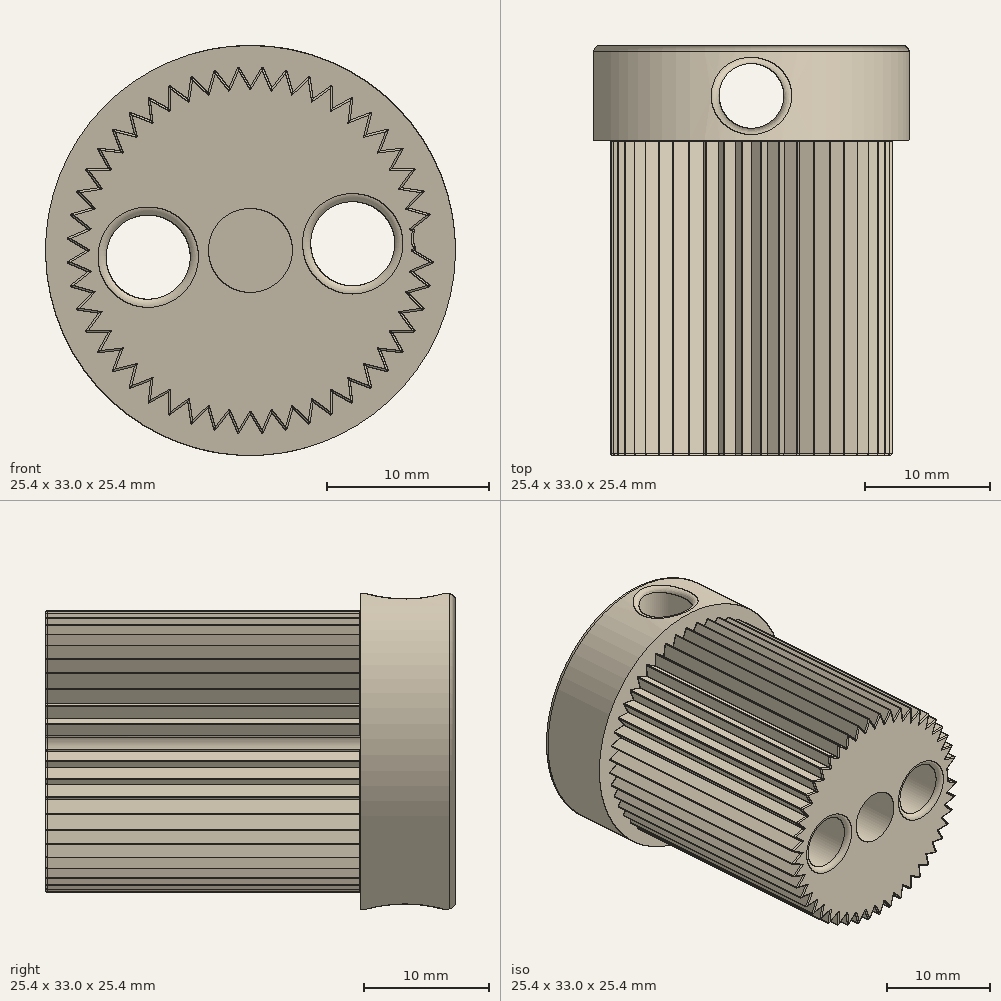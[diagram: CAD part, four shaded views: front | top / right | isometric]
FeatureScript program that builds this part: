
annotation { "Feature Type Name" : "Feature", "Feature Type Description" : "" }
export const myFeature = defineFeature(function(context is Context, id is Id, definition is map)
    precondition{}
    {
        {
            var Q0;
            Q0=qCreatedBy(makeId("Front.planeOp"),FACE);
            var sketch = newSketch(context, id + "F0", { "sketchPlane" : qUnion([Q0])});
            skCircle(sketch, "E0", {"center": v(0, 0) * mm, "radius": 10.16 * mm, "construction": true});
            skCircle(sketch, "E1", {"center": v(0, 0) * mm, "radius": 11.43 * mm, "construction": true});
            skLineSegment(sketch, "E2", {"start": v(0, 0) * mm, "end": v(24.31, 0) * mm, "construction": true});
            skLineSegment(sketch, "E3", {"start": v(0, 0) * mm, "end": v(24.33, -1.6) * mm, "construction": true});
            skLineSegment(sketch, "E4", {"start": v(0, 0) * mm, "end": v(10.07, -1.33) * mm, "construction": true});
            skLineSegment(sketch, "E5", {"start": v(9.53, 0) * mm, "end": v(10.16, 0) * mm});
            skLineSegment(sketch, "E6", {"start": v(10.16, 0) * mm, "end": v(11.4, -0.75) * mm});
            skLineSegment(sketch, "E7", {"start": v(10.07, -1.33) * mm, "end": v(9.44, -1.24) * mm});
            skLineSegment(sketch, "E8", {"start": v(0, 0) * mm, "end": v(9.53, 0) * mm});
            skLineSegment(sketch, "E9", {"start": v(0, 0) * mm, "end": v(9.44, -1.24) * mm});
            skLineSegment(sketch, "E10", {"start": v(11.4, -0.75) * mm, "end": v(10.07, -1.33) * mm});
            skLineSegment(sketch, "E11.trimOffspring", {"start": v(11.33, -1.5) * mm, "end": v(23.43, -3.08) * mm, "construction": true});
            skPoint(sketch, "E12.orphan", {"position": v(10.16, -1.34) * mm});
            skLineSegment(sketch, "E13", {"start": v(17.07, 1.12) * mm, "end": v(-16.43, -1.08) * mm, "construction": true});
            skCircle(sketch, "E14", {"center": v(0, 0) * mm, "radius": 6.35 * mm, "construction": true});
            skCircle(sketch, "E15", {"center": v(-6.34, -0.42) * mm, "radius": 2.6 * mm});
            skCircle(sketch, "E16", {"center": v(6.34, 0.42) * mm, "radius": 2.6 * mm});
            skSolve(sketch);
        }
        {
            var Q0;
            Q0=makeQuery(id+"F0.imprint","IMPRINT",FACE,{"disambiguationData":[TD([[makeQuery(id+"F0.imprint","IMPRINT",EDGE,{"derivedFrom":sQuery(id+"F0.wireOp",EDGE,"E5")}),-1.0]])]});
            var Q1;
            {var subQ0=sQuery(id+"F0.wireOp",EDGE,"E16");var subQ1=sQuery(id+"F0.wireOp",EDGE,"E8");var subQ2=makeQuery(id+"F0.imprint","INTERSECT",VERTEX,{"disambiguationData":[OD(0.0)],"derivedFrom":[subQ1,subQ0]});Q1=makeQuery(id+"F0.imprint","IMPRINT",FACE,{"disambiguationData":[TD([[makeQuery(id+"F0.imprint","IMPRINT",EDGE,{"disambiguationData":[TD([[subQ2,-1.0]])],"derivedFrom":subQ1}),-1.0]])]});}
            var Q2;
            {var subQ0=sQuery(id+"F0.wireOp",EDGE,"E9");var subQ1=sQuery(id+"F0.wireOp",EDGE,"E8");var subQ2=makeQuery(id+"F0.imprint","INTERSECT",VERTEX,{"derivedFrom":[subQ1,subQ0]});Q2=makeQuery(id+"F0.imprint","IMPRINT",FACE,{"disambiguationData":[TD([[makeQuery(id+"F0.imprint","IMPRINT",EDGE,{"disambiguationData":[TD([[subQ2,-1.0]])],"derivedFrom":subQ1}),-1.0]])]});}
            extrude(context, id + "F1", {"entities" : qUnion([Q0, Q1, Q2]), "depth" : 25.4 * mm});
        }
        {
            var Q0;
            Q0=makeQuery(id+"F1.opExtrude","CAP_EDGE",EDGE,{"disambiguationData":[OSD([sQuery(id+"F0.wireOp",EDGE,"E6")])],"isStart":false});
            var Q1;
            Q1=makeQuery(id+"F1.opExtrude","CAP_EDGE",EDGE,{"disambiguationData":[OSD([sQuery(id+"F0.wireOp",EDGE,"E10")])],"isStart":false});
            var Q2;
            Q2=makeQuery(id+"F1.opExtrude","CAP_EDGE",EDGE,{"disambiguationData":[OSD([sQuery(id+"F0.wireOp",EDGE,"E6")])],"isStart":true});
            var Q3;
            Q3=makeQuery(id+"F1.opExtrude","CAP_EDGE",EDGE,{"disambiguationData":[OSD([sQuery(id+"F0.wireOp",EDGE,"E10")])],"isStart":true});
            fillet(context, id + "F2", {"entities" : qUnion([Q0, Q1, Q2, Q3]), "radius" : 0.13 * mm, "tangentPropagation" : true, "allowEdgeOverflow" : false});
        }
        {
            var Q0;
            Q0=makeQuery(id+"F1.opExtrude","SWEPT_EDGE",EDGE,{"disambiguationData":[OSD([sQuery(id+"F0.wireOp",EDGE,"E6"),sQuery(id+"F0.wireOp",EDGE,"E10")])]});
            fillet(context, id + "F3", {"entities" : qUnion([Q0]), "radius" : 0.05 * mm, "tangentPropagation" : true, "allowEdgeOverflow" : false});
        }
        {
            var Q0;
            Q0=makeQuery(id+"F1.opExtrude","SWEPT_BODY",BODY,{"disambiguationData":[OSD([sQuery(id+"F0.wireOp",EDGE,"E5"),sQuery(id+"F0.wireOp",EDGE,"E6"),sQuery(id+"F0.wireOp",EDGE,"gNua0P1m-RBOV-57z6-Uz5b-c0gyhJW3q2aB"),sQuery(id+"F0.wireOp",EDGE,"E7"),sQuery(id+"F0.wireOp",EDGE,"E8"),sQuery(id+"F0.wireOp",EDGE,"E9")])]});
            var Q1;
            Q1=makeQuery(id+"F1.opExtrude","SWEPT_EDGE",EDGE,{"disambiguationData":[OSD([sQuery(id+"F0.wireOp",EDGE,"E8"),sQuery(id+"F0.wireOp",EDGE,"E9")])]});
            circularPattern(context, id + "F4", {"operationType" : NewBodyOperationType.ADD, "entities" : qUnion([Q0]), "axis" : qUnion([Q1]), "angle" : 360 * degree, "instanceCount" : 48, "equalSpace" : true});
        }
        {
            var Q0;
            {var subQ0=makeQuery(id+"F1.opExtrude","CAP_FACE",FACE,{"disambiguationData":[OSD([sQuery(id+"F0.wireOp",EDGE,"E5"),sQuery(id+"F0.wireOp",EDGE,"E6"),sQuery(id+"F0.wireOp",EDGE,"E7"),sQuery(id+"F0.wireOp",EDGE,"E8"),sQuery(id+"F0.wireOp",EDGE,"E9"),sQuery(id+"F0.wireOp",EDGE,"E10")])],"isStart":true});Q0=makeQuery(id+"F4.boolean.opBoolean","MERGE",FACE,{"derivedFrom":[subQ0,makeQuery(id+"F4.opPattern","COPY",FACE,{"derivedFrom":subQ0,"instanceName":"1"}),makeQuery(id+"F4.opPattern","COPY",FACE,{"derivedFrom":subQ0,"instanceName":"2"}),makeQuery(id+"F4.opPattern","COPY",FACE,{"derivedFrom":subQ0,"instanceName":"3"}),makeQuery(id+"F4.opPattern","COPY",FACE,{"derivedFrom":subQ0,"instanceName":"4"}),makeQuery(id+"F4.opPattern","COPY",FACE,{"derivedFrom":subQ0,"instanceName":"5"}),makeQuery(id+"F4.opPattern","COPY",FACE,{"derivedFrom":subQ0,"instanceName":"6"}),makeQuery(id+"F4.opPattern","COPY",FACE,{"derivedFrom":subQ0,"instanceName":"7"}),makeQuery(id+"F4.opPattern","COPY",FACE,{"derivedFrom":subQ0,"instanceName":"8"}),makeQuery(id+"F4.opPattern","COPY",FACE,{"derivedFrom":subQ0,"instanceName":"9"}),makeQuery(id+"F4.opPattern","COPY",FACE,{"derivedFrom":subQ0,"instanceName":"10"}),makeQuery(id+"F4.opPattern","COPY",FACE,{"derivedFrom":subQ0,"instanceName":"11"}),makeQuery(id+"F4.opPattern","COPY",FACE,{"derivedFrom":subQ0,"instanceName":"12"}),makeQuery(id+"F4.opPattern","COPY",FACE,{"derivedFrom":subQ0,"instanceName":"13"}),makeQuery(id+"F4.opPattern","COPY",FACE,{"derivedFrom":subQ0,"instanceName":"14"}),makeQuery(id+"F4.opPattern","COPY",FACE,{"derivedFrom":subQ0,"instanceName":"15"}),makeQuery(id+"F4.opPattern","COPY",FACE,{"derivedFrom":subQ0,"instanceName":"16"}),makeQuery(id+"F4.opPattern","COPY",FACE,{"derivedFrom":subQ0,"instanceName":"17"}),makeQuery(id+"F4.opPattern","COPY",FACE,{"derivedFrom":subQ0,"instanceName":"18"}),makeQuery(id+"F4.opPattern","COPY",FACE,{"derivedFrom":subQ0,"instanceName":"19"}),makeQuery(id+"F4.opPattern","COPY",FACE,{"derivedFrom":subQ0,"instanceName":"20"}),makeQuery(id+"F4.opPattern","COPY",FACE,{"derivedFrom":subQ0,"instanceName":"21"}),makeQuery(id+"F4.opPattern","COPY",FACE,{"derivedFrom":subQ0,"instanceName":"22"}),makeQuery(id+"F4.opPattern","COPY",FACE,{"derivedFrom":subQ0,"instanceName":"23"}),makeQuery(id+"F4.opPattern","COPY",FACE,{"derivedFrom":subQ0,"instanceName":"24"}),makeQuery(id+"F4.opPattern","COPY",FACE,{"derivedFrom":subQ0,"instanceName":"25"}),makeQuery(id+"F4.opPattern","COPY",FACE,{"derivedFrom":subQ0,"instanceName":"26"}),makeQuery(id+"F4.opPattern","COPY",FACE,{"derivedFrom":subQ0,"instanceName":"27"}),makeQuery(id+"F4.opPattern","COPY",FACE,{"derivedFrom":subQ0,"instanceName":"28"}),makeQuery(id+"F4.opPattern","COPY",FACE,{"derivedFrom":subQ0,"instanceName":"29"}),makeQuery(id+"F4.opPattern","COPY",FACE,{"derivedFrom":subQ0,"instanceName":"30"}),makeQuery(id+"F4.opPattern","COPY",FACE,{"derivedFrom":subQ0,"instanceName":"31"}),makeQuery(id+"F4.opPattern","COPY",FACE,{"derivedFrom":subQ0,"instanceName":"32"}),makeQuery(id+"F4.opPattern","COPY",FACE,{"derivedFrom":subQ0,"instanceName":"33"}),makeQuery(id+"F4.opPattern","COPY",FACE,{"derivedFrom":subQ0,"instanceName":"34"}),makeQuery(id+"F4.opPattern","COPY",FACE,{"derivedFrom":subQ0,"instanceName":"35"}),makeQuery(id+"F4.opPattern","COPY",FACE,{"derivedFrom":subQ0,"instanceName":"36"}),makeQuery(id+"F4.opPattern","COPY",FACE,{"derivedFrom":subQ0,"instanceName":"37"}),makeQuery(id+"F4.opPattern","COPY",FACE,{"derivedFrom":subQ0,"instanceName":"38"}),makeQuery(id+"F4.opPattern","COPY",FACE,{"derivedFrom":subQ0,"instanceName":"39"}),makeQuery(id+"F4.opPattern","COPY",FACE,{"derivedFrom":subQ0,"instanceName":"40"}),makeQuery(id+"F4.opPattern","COPY",FACE,{"derivedFrom":subQ0,"instanceName":"41"}),makeQuery(id+"F4.opPattern","COPY",FACE,{"derivedFrom":subQ0,"instanceName":"42"}),makeQuery(id+"F4.opPattern","COPY",FACE,{"derivedFrom":subQ0,"instanceName":"43"}),makeQuery(id+"F4.opPattern","COPY",FACE,{"derivedFrom":subQ0,"instanceName":"44"}),makeQuery(id+"F4.opPattern","COPY",FACE,{"derivedFrom":subQ0,"instanceName":"45"}),makeQuery(id+"F4.opPattern","COPY",FACE,{"derivedFrom":subQ0,"instanceName":"46"}),makeQuery(id+"F4.opPattern","COPY",FACE,{"derivedFrom":subQ0,"instanceName":"47"})]});}
            var sketch = newSketch(context, id + "F5", { "sketchPlane" : qUnion([Q0])});
            skCircle(sketch, "E17", {"center": v(0, 0) * mm, "radius": 12.7 * mm});
            skSolve(sketch);
        }
        {
            var Q0;
            Q0=makeQuery(id+"F5.imprint","IMPRINT",FACE,{"disambiguationData":[TD([[makeQuery(id+"F5.imprint","IMPRINT",EDGE,{"derivedFrom":sQuery(id+"F5.wireOp",EDGE,"E17")}),1.0]])]});
            var Q1;
            {var subQ0=sQuery(id+"F0.wireOp",EDGE,"E10");var subQ1=sQuery(id+"F0.wireOp",EDGE,"E6");var subQ2=makeQuery(id+"F1.opExtrude","CAP_FACE",FACE,{"disambiguationData":[OSD([sQuery(id+"F0.wireOp",EDGE,"E5"),subQ1,sQuery(id+"F0.wireOp",EDGE,"E7"),sQuery(id+"F0.wireOp",EDGE,"E8"),sQuery(id+"F0.wireOp",EDGE,"E9"),subQ0])],"isStart":true});var subQ4=makeQuery(id+"F2.opFillet","BLEND_EDGE",EDGE,{"blendedFrom":[makeQuery(id+"F1.opExtrude","CAP_EDGE",EDGE,{"disambiguationData":[OSD([subQ1])],"isStart":true}),subQ2],"blendedInto":[subQ2]});Q1=makeQuery(id+"F5.imprint","IMPRINT",FACE,{"disambiguationData":[TD([[makeQuery(id+"F5.imprint","IMPRINT",EDGE,{"derivedFrom":subQ4}),1.0]])]});}
            var Q2;
            Q2=sQuery(id+"F5.wireOp",EDGE,"E17");
            extrude(context, id + "F6", {"entities" : qUnion([Q0, Q1]), "operationType" : NewBodyOperationType.ADD, "surfaceEntities" : qUnion([Q2]), "depth" : 7.62 * mm});
        }
        {
            var Q0;
            Q0=makeQuery(id+"F0.imprint","IMPRINT",FACE,{"disambiguationData":[TD([[makeQuery(id+"F0.imprint","IMPRINT",EDGE,{"derivedFrom":sQuery(id+"F0.wireOp",EDGE,"E15")}),1.0]])]});
            var Q1;
            {var subQ0=sQuery(id+"F0.wireOp",EDGE,"E16");var subQ1=sQuery(id+"F0.wireOp",EDGE,"E8");var subQ2=makeQuery(id+"F0.imprint","INTERSECT",VERTEX,{"disambiguationData":[OD(0.0)],"derivedFrom":[subQ1,subQ0]});Q1=makeQuery(id+"F0.imprint","IMPRINT",FACE,{"disambiguationData":[TD([[makeQuery(id+"F0.imprint","IMPRINT",EDGE,{"disambiguationData":[TD([[subQ2,-1.0]])],"derivedFrom":subQ1}),1.0]])]});}
            var Q2;
            {var subQ0=sQuery(id+"F0.wireOp",EDGE,"E16");var subQ1=sQuery(id+"F0.wireOp",EDGE,"E8");var subQ2=makeQuery(id+"F0.imprint","INTERSECT",VERTEX,{"disambiguationData":[OD(0.0)],"derivedFrom":[subQ1,subQ0]});Q2=makeQuery(id+"F0.imprint","IMPRINT",FACE,{"disambiguationData":[TD([[makeQuery(id+"F0.imprint","IMPRINT",EDGE,{"disambiguationData":[TD([[subQ2,-1.0]])],"derivedFrom":subQ1}),-1.0]])]});}
            var Q3;
            {var subQ0=sQuery(id+"F0.wireOp",EDGE,"E16");var subQ1=sQuery(id+"F0.wireOp",EDGE,"E9");var subQ2=makeQuery(id+"F0.imprint","INTERSECT",VERTEX,{"disambiguationData":[OD(0.0)],"derivedFrom":[subQ1,subQ0]});Q3=makeQuery(id+"F0.imprint","IMPRINT",FACE,{"disambiguationData":[TD([[makeQuery(id+"F0.imprint","IMPRINT",EDGE,{"disambiguationData":[TD([[subQ2,-1.0]])],"derivedFrom":subQ1}),-1.0]])]});}
            extrude(context, id + "F7", {"entities" : qUnion([Q0, Q1, Q2, Q3]), "operationType" : NewBodyOperationType.REMOVE, "endBound" : BoundingType.SYMMETRIC, "depth" : 50.8 * mm});
        }
        {
            var Q0;
            {var subQ0=makeQuery(id+"F1.opExtrude","CAP_FACE",FACE,{"disambiguationData":[OSD([sQuery(id+"F0.wireOp",EDGE,"E5"),sQuery(id+"F0.wireOp",EDGE,"E6"),sQuery(id+"F0.wireOp",EDGE,"gNua0P1m-RBOV-57z6-Uz5b-c0gyhJW3q2aB"),sQuery(id+"F0.wireOp",EDGE,"E7"),sQuery(id+"F0.wireOp",EDGE,"E8"),sQuery(id+"F0.wireOp",EDGE,"E9")])],"isStart":false});Q0=makeQuery(id+"F4.boolean.opBoolean","MERGE",FACE,{"derivedFrom":[subQ0,makeQuery(id+"F4.opPattern","COPY",FACE,{"derivedFrom":subQ0,"instanceName":"1"}),makeQuery(id+"F4.opPattern","COPY",FACE,{"derivedFrom":subQ0,"instanceName":"2"}),makeQuery(id+"F4.opPattern","COPY",FACE,{"derivedFrom":subQ0,"instanceName":"3"}),makeQuery(id+"F4.opPattern","COPY",FACE,{"derivedFrom":subQ0,"instanceName":"4"}),makeQuery(id+"F4.opPattern","COPY",FACE,{"derivedFrom":subQ0,"instanceName":"5"}),makeQuery(id+"F4.opPattern","COPY",FACE,{"derivedFrom":subQ0,"instanceName":"6"}),makeQuery(id+"F4.opPattern","COPY",FACE,{"derivedFrom":subQ0,"instanceName":"7"}),makeQuery(id+"F4.opPattern","COPY",FACE,{"derivedFrom":subQ0,"instanceName":"8"}),makeQuery(id+"F4.opPattern","COPY",FACE,{"derivedFrom":subQ0,"instanceName":"9"}),makeQuery(id+"F4.opPattern","COPY",FACE,{"derivedFrom":subQ0,"instanceName":"10"}),makeQuery(id+"F4.opPattern","COPY",FACE,{"derivedFrom":subQ0,"instanceName":"11"}),makeQuery(id+"F4.opPattern","COPY",FACE,{"derivedFrom":subQ0,"instanceName":"12"}),makeQuery(id+"F4.opPattern","COPY",FACE,{"derivedFrom":subQ0,"instanceName":"13"}),makeQuery(id+"F4.opPattern","COPY",FACE,{"derivedFrom":subQ0,"instanceName":"14"}),makeQuery(id+"F4.opPattern","COPY",FACE,{"derivedFrom":subQ0,"instanceName":"15"}),makeQuery(id+"F4.opPattern","COPY",FACE,{"derivedFrom":subQ0,"instanceName":"16"}),makeQuery(id+"F4.opPattern","COPY",FACE,{"derivedFrom":subQ0,"instanceName":"17"}),makeQuery(id+"F4.opPattern","COPY",FACE,{"derivedFrom":subQ0,"instanceName":"18"}),makeQuery(id+"F4.opPattern","COPY",FACE,{"derivedFrom":subQ0,"instanceName":"19"}),makeQuery(id+"F4.opPattern","COPY",FACE,{"derivedFrom":subQ0,"instanceName":"20"}),makeQuery(id+"F4.opPattern","COPY",FACE,{"derivedFrom":subQ0,"instanceName":"21"}),makeQuery(id+"F4.opPattern","COPY",FACE,{"derivedFrom":subQ0,"instanceName":"22"}),makeQuery(id+"F4.opPattern","COPY",FACE,{"derivedFrom":subQ0,"instanceName":"23"}),makeQuery(id+"F4.opPattern","COPY",FACE,{"derivedFrom":subQ0,"instanceName":"24"}),makeQuery(id+"F4.opPattern","COPY",FACE,{"derivedFrom":subQ0,"instanceName":"25"}),makeQuery(id+"F4.opPattern","COPY",FACE,{"derivedFrom":subQ0,"instanceName":"26"}),makeQuery(id+"F4.opPattern","COPY",FACE,{"derivedFrom":subQ0,"instanceName":"27"}),makeQuery(id+"F4.opPattern","COPY",FACE,{"derivedFrom":subQ0,"instanceName":"28"}),makeQuery(id+"F4.opPattern","COPY",FACE,{"derivedFrom":subQ0,"instanceName":"29"}),makeQuery(id+"F4.opPattern","COPY",FACE,{"derivedFrom":subQ0,"instanceName":"30"}),makeQuery(id+"F4.opPattern","COPY",FACE,{"derivedFrom":subQ0,"instanceName":"31"}),makeQuery(id+"F4.opPattern","COPY",FACE,{"derivedFrom":subQ0,"instanceName":"32"}),makeQuery(id+"F4.opPattern","COPY",FACE,{"derivedFrom":subQ0,"instanceName":"33"}),makeQuery(id+"F4.opPattern","COPY",FACE,{"derivedFrom":subQ0,"instanceName":"34"}),makeQuery(id+"F4.opPattern","COPY",FACE,{"derivedFrom":subQ0,"instanceName":"35"}),makeQuery(id+"F4.opPattern","COPY",FACE,{"derivedFrom":subQ0,"instanceName":"36"}),makeQuery(id+"F4.opPattern","COPY",FACE,{"derivedFrom":subQ0,"instanceName":"37"}),makeQuery(id+"F4.opPattern","COPY",FACE,{"derivedFrom":subQ0,"instanceName":"38"}),makeQuery(id+"F4.opPattern","COPY",FACE,{"derivedFrom":subQ0,"instanceName":"39"}),makeQuery(id+"F4.opPattern","COPY",FACE,{"derivedFrom":subQ0,"instanceName":"40"}),makeQuery(id+"F4.opPattern","COPY",FACE,{"derivedFrom":subQ0,"instanceName":"41"}),makeQuery(id+"F4.opPattern","COPY",FACE,{"derivedFrom":subQ0,"instanceName":"42"}),makeQuery(id+"F4.opPattern","COPY",FACE,{"derivedFrom":subQ0,"instanceName":"43"}),makeQuery(id+"F4.opPattern","COPY",FACE,{"derivedFrom":subQ0,"instanceName":"44"}),makeQuery(id+"F4.opPattern","COPY",FACE,{"derivedFrom":subQ0,"instanceName":"45"}),makeQuery(id+"F4.opPattern","COPY",FACE,{"derivedFrom":subQ0,"instanceName":"46"}),makeQuery(id+"F4.opPattern","COPY",FACE,{"derivedFrom":subQ0,"instanceName":"47"}),makeQuery(id+"F4.opPattern","COPY",FACE,{"derivedFrom":subQ0,"instanceName":"48"}),makeQuery(id+"F4.opPattern","COPY",FACE,{"derivedFrom":subQ0,"instanceName":"49"}),makeQuery(id+"F4.opPattern","COPY",FACE,{"derivedFrom":subQ0,"instanceName":"50"}),makeQuery(id+"F4.opPattern","COPY",FACE,{"derivedFrom":subQ0,"instanceName":"51"}),makeQuery(id+"F4.opPattern","COPY",FACE,{"derivedFrom":subQ0,"instanceName":"52"}),makeQuery(id+"F4.opPattern","COPY",FACE,{"derivedFrom":subQ0,"instanceName":"53"}),makeQuery(id+"F4.opPattern","COPY",FACE,{"derivedFrom":subQ0,"instanceName":"54"}),makeQuery(id+"F4.opPattern","COPY",FACE,{"derivedFrom":subQ0,"instanceName":"55"}),makeQuery(id+"F4.opPattern","COPY",FACE,{"derivedFrom":subQ0,"instanceName":"56"}),makeQuery(id+"F4.opPattern","COPY",FACE,{"derivedFrom":subQ0,"instanceName":"57"}),makeQuery(id+"F4.opPattern","COPY",FACE,{"derivedFrom":subQ0,"instanceName":"58"}),makeQuery(id+"F4.opPattern","COPY",FACE,{"derivedFrom":subQ0,"instanceName":"59"}),makeQuery(id+"F4.opPattern","COPY",FACE,{"derivedFrom":subQ0,"instanceName":"60"}),makeQuery(id+"F4.opPattern","COPY",FACE,{"derivedFrom":subQ0,"instanceName":"61"}),makeQuery(id+"F4.opPattern","COPY",FACE,{"derivedFrom":subQ0,"instanceName":"62"}),makeQuery(id+"F4.opPattern","COPY",FACE,{"derivedFrom":subQ0,"instanceName":"63"}),makeQuery(id+"F4.opPattern","COPY",FACE,{"derivedFrom":subQ0,"instanceName":"64"}),makeQuery(id+"F4.opPattern","COPY",FACE,{"derivedFrom":subQ0,"instanceName":"65"}),makeQuery(id+"F4.opPattern","COPY",FACE,{"derivedFrom":subQ0,"instanceName":"66"}),makeQuery(id+"F4.opPattern","COPY",FACE,{"derivedFrom":subQ0,"instanceName":"67"}),makeQuery(id+"F4.opPattern","COPY",FACE,{"derivedFrom":subQ0,"instanceName":"68"}),makeQuery(id+"F4.opPattern","COPY",FACE,{"derivedFrom":subQ0,"instanceName":"69"}),makeQuery(id+"F4.opPattern","COPY",FACE,{"derivedFrom":subQ0,"instanceName":"70"}),makeQuery(id+"F4.opPattern","COPY",FACE,{"derivedFrom":subQ0,"instanceName":"71"})]});}
            var sketch = newSketch(context, id + "F8", { "sketchPlane" : qUnion([Q0])});
            skCircle(sketch, "E18", {"center": v(0, 0) * mm, "radius": 9.59 * mm});
            skLineSegment(sketch, "E19", {"start": v(0, 0) * mm, "end": v(11.91, 0) * mm, "construction": true});
            skLineSegment(sketch, "E20", {"start": v(0, 0) * mm, "end": v(12.83, 0.84) * mm, "construction": true});
            skCircle(sketch, "E21", {"center": v(10.07, 0.66) * mm, "radius": 0.5 * mm});
            skCircle(sketch, "E22", {"center": v(0, 0) * mm, "radius": 2.6 * mm});
            skSolve(sketch);
        }
        {
            var Q0;
            {var subQ0=makeQuery(id+"F1.opExtrude","CAP_FACE",FACE,{"disambiguationData":[OSD([sQuery(id+"F0.wireOp",EDGE,"E5"),sQuery(id+"F0.wireOp",EDGE,"E6"),sQuery(id+"F0.wireOp",EDGE,"E7"),sQuery(id+"F0.wireOp",EDGE,"E8"),sQuery(id+"F0.wireOp",EDGE,"E9"),sQuery(id+"F0.wireOp",EDGE,"E10")])],"isStart":false});Q0=makeQuery(id+"F4.boolean.opBoolean","MERGE",FACE,{"derivedFrom":[subQ0,makeQuery(id+"F4.opPattern","COPY",FACE,{"derivedFrom":subQ0,"instanceName":"1"}),makeQuery(id+"F4.opPattern","COPY",FACE,{"derivedFrom":subQ0,"instanceName":"2"}),makeQuery(id+"F4.opPattern","COPY",FACE,{"derivedFrom":subQ0,"instanceName":"3"}),makeQuery(id+"F4.opPattern","COPY",FACE,{"derivedFrom":subQ0,"instanceName":"4"}),makeQuery(id+"F4.opPattern","COPY",FACE,{"derivedFrom":subQ0,"instanceName":"5"}),makeQuery(id+"F4.opPattern","COPY",FACE,{"derivedFrom":subQ0,"instanceName":"6"}),makeQuery(id+"F4.opPattern","COPY",FACE,{"derivedFrom":subQ0,"instanceName":"7"}),makeQuery(id+"F4.opPattern","COPY",FACE,{"derivedFrom":subQ0,"instanceName":"8"}),makeQuery(id+"F4.opPattern","COPY",FACE,{"derivedFrom":subQ0,"instanceName":"9"}),makeQuery(id+"F4.opPattern","COPY",FACE,{"derivedFrom":subQ0,"instanceName":"10"}),makeQuery(id+"F4.opPattern","COPY",FACE,{"derivedFrom":subQ0,"instanceName":"11"}),makeQuery(id+"F4.opPattern","COPY",FACE,{"derivedFrom":subQ0,"instanceName":"12"}),makeQuery(id+"F4.opPattern","COPY",FACE,{"derivedFrom":subQ0,"instanceName":"13"}),makeQuery(id+"F4.opPattern","COPY",FACE,{"derivedFrom":subQ0,"instanceName":"14"}),makeQuery(id+"F4.opPattern","COPY",FACE,{"derivedFrom":subQ0,"instanceName":"15"}),makeQuery(id+"F4.opPattern","COPY",FACE,{"derivedFrom":subQ0,"instanceName":"16"}),makeQuery(id+"F4.opPattern","COPY",FACE,{"derivedFrom":subQ0,"instanceName":"17"}),makeQuery(id+"F4.opPattern","COPY",FACE,{"derivedFrom":subQ0,"instanceName":"18"}),makeQuery(id+"F4.opPattern","COPY",FACE,{"derivedFrom":subQ0,"instanceName":"19"}),makeQuery(id+"F4.opPattern","COPY",FACE,{"derivedFrom":subQ0,"instanceName":"20"}),makeQuery(id+"F4.opPattern","COPY",FACE,{"derivedFrom":subQ0,"instanceName":"21"}),makeQuery(id+"F4.opPattern","COPY",FACE,{"derivedFrom":subQ0,"instanceName":"22"}),makeQuery(id+"F4.opPattern","COPY",FACE,{"derivedFrom":subQ0,"instanceName":"23"}),makeQuery(id+"F4.opPattern","COPY",FACE,{"derivedFrom":subQ0,"instanceName":"24"}),makeQuery(id+"F4.opPattern","COPY",FACE,{"derivedFrom":subQ0,"instanceName":"25"}),makeQuery(id+"F4.opPattern","COPY",FACE,{"derivedFrom":subQ0,"instanceName":"26"}),makeQuery(id+"F4.opPattern","COPY",FACE,{"derivedFrom":subQ0,"instanceName":"27"}),makeQuery(id+"F4.opPattern","COPY",FACE,{"derivedFrom":subQ0,"instanceName":"28"}),makeQuery(id+"F4.opPattern","COPY",FACE,{"derivedFrom":subQ0,"instanceName":"29"}),makeQuery(id+"F4.opPattern","COPY",FACE,{"derivedFrom":subQ0,"instanceName":"30"}),makeQuery(id+"F4.opPattern","COPY",FACE,{"derivedFrom":subQ0,"instanceName":"31"}),makeQuery(id+"F4.opPattern","COPY",FACE,{"derivedFrom":subQ0,"instanceName":"32"}),makeQuery(id+"F4.opPattern","COPY",FACE,{"derivedFrom":subQ0,"instanceName":"33"}),makeQuery(id+"F4.opPattern","COPY",FACE,{"derivedFrom":subQ0,"instanceName":"34"}),makeQuery(id+"F4.opPattern","COPY",FACE,{"derivedFrom":subQ0,"instanceName":"35"}),makeQuery(id+"F4.opPattern","COPY",FACE,{"derivedFrom":subQ0,"instanceName":"36"}),makeQuery(id+"F4.opPattern","COPY",FACE,{"derivedFrom":subQ0,"instanceName":"37"}),makeQuery(id+"F4.opPattern","COPY",FACE,{"derivedFrom":subQ0,"instanceName":"38"}),makeQuery(id+"F4.opPattern","COPY",FACE,{"derivedFrom":subQ0,"instanceName":"39"}),makeQuery(id+"F4.opPattern","COPY",FACE,{"derivedFrom":subQ0,"instanceName":"40"}),makeQuery(id+"F4.opPattern","COPY",FACE,{"derivedFrom":subQ0,"instanceName":"41"}),makeQuery(id+"F4.opPattern","COPY",FACE,{"derivedFrom":subQ0,"instanceName":"42"}),makeQuery(id+"F4.opPattern","COPY",FACE,{"derivedFrom":subQ0,"instanceName":"43"}),makeQuery(id+"F4.opPattern","COPY",FACE,{"derivedFrom":subQ0,"instanceName":"44"}),makeQuery(id+"F4.opPattern","COPY",FACE,{"derivedFrom":subQ0,"instanceName":"45"}),makeQuery(id+"F4.opPattern","COPY",FACE,{"derivedFrom":subQ0,"instanceName":"46"}),makeQuery(id+"F4.opPattern","COPY",FACE,{"derivedFrom":subQ0,"instanceName":"47"})]});}
            var sketch = newSketch(context, id + "F9", { "sketchPlane" : qUnion([Q0])});
            skCircle(sketch, "E23", {"center": v(11.13, 0.73) * mm, "radius": 1.05 * mm});
            skSolve(sketch);
        }
        {
            var Q0;
            Q0=qSketchRegion(id+"F9",true);
            var Q1;
            Q1=makeQuery(id+"F6.opExtrude","CAP_FACE",FACE,{"disambiguationData":[OSD([sQuery(id+"F5.wireOp",EDGE,"E17")])],"isStart":true});
            extrude(context, id + "F10", {"entities" : qUnion([Q0]), "operationType" : NewBodyOperationType.REMOVE, "endBound" : BoundingType.UP_TO_SURFACE, "oppositeDirection" : true, "endBoundEntityFace" : qUnion([Q1]), "depth" : 25.4 * mm});
        }
        {
            var Q0;
            Q0=makeQuery(id+"F8.imprint","IMPRINT",FACE,{"disambiguationData":[TD([[makeQuery(id+"F8.imprint","IMPRINT",EDGE,{"derivedFrom":sQuery(id+"F8.wireOp",EDGE,"E22")}),1.0]])]});
            var Q1;
            Q1=sQuery(id+"F8.wireOp",EDGE,"E22");
            extrude(context, id + "F11", {"entities" : qUnion([Q0]), "operationType" : NewBodyOperationType.REMOVE, "surfaceEntities" : qUnion([Q1]), "oppositeDirection" : true, "depth" : 22.86 * mm});
        }
        {
            var Q0;
            Q0=makeQuery(id+"F10.boolean.opBoolean","INTERSECT",EDGE,{"derivedFrom":[makeQuery(id+"F4.opPattern","COPY",FACE,{"derivedFrom":makeQuery(id+"F1.opExtrude","SWEPT_FACE",FACE,{"disambiguationData":[OSD([sQuery(id+"F0.wireOp",EDGE,"E6")])]}),"instanceName":"47"}),makeQuery(id+"F10.opExtrude","SWEPT_FACE",FACE,{"disambiguationData":[OSD([sQuery(id+"F9.wireOp",EDGE,"E23")])]})]});
            var Q1;
            Q1=makeQuery(id+"F10.boolean.opBoolean","COPY",EDGE,{"derivedFrom":makeQuery(id+"F10.opExtrude","CAP_EDGE",EDGE,{"disambiguationData":[OSD([sQuery(id+"F9.wireOp",EDGE,"E23")])],"isStart":true})});
            fillet(context, id + "F12", {"entities" : qUnion([Q0, Q1]), "radius" : 0.13 * mm, "tangentPropagation" : true, "allowEdgeOverflow" : false});
        }
        {
            var Q0;
            Q0=qCreatedBy(makeId("Top.planeOp"),FACE);
            var sketch = newSketch(context, id + "F13", { "sketchPlane" : qUnion([Q0])});
            skLineSegment(sketch, "E24", {"start": v(-12.7, 0) * mm, "end": v(-12.7, 7.62) * mm});
            skLineSegment(sketch, "E25", {"start": v(12.7, 7.62) * mm, "end": v(12.7, 0) * mm});
            skCircle(sketch, "E26", {"center": v(0, 3.56) * mm, "radius": 2.6 * mm});
            skSolve(sketch);
        }
        {
            var Q0;
            Q0=qSketchRegion(id+"F13",true);
            var Q1;
            Q1=sQuery(id+"F13.wireOp",EDGE,"E26");
            extrude(context, id + "F14", {"entities" : qUnion([Q0]), "operationType" : NewBodyOperationType.REMOVE, "surfaceEntities" : qUnion([Q1]), "endBound" : BoundingType.SYMMETRIC, "oppositeDirection" : true, "depth" : 25.4 * mm});
        }
        {
            var Q0;
            Q0=makeQuery(id+"F7.boolean.opBoolean","COPY",EDGE,{"derivedFrom":makeQuery(id+"F7.opExtrude","CAP_EDGE",EDGE,{"disambiguationData":[OSD([sQuery(id+"F0.wireOp",EDGE,"E16")])],"isStart":true})});
            var Q1;
            Q1=makeQuery(id+"F7.boolean.opBoolean","COPY",EDGE,{"derivedFrom":makeQuery(id+"F7.opExtrude","CAP_EDGE",EDGE,{"disambiguationData":[OSD([sQuery(id+"F0.wireOp",EDGE,"E15")])],"isStart":true})});
            var Q2;
            {var subQ0=makeQuery(id+"F1.opExtrude","CAP_FACE",FACE,{"disambiguationData":[OSD([sQuery(id+"F0.wireOp",EDGE,"E5"),sQuery(id+"F0.wireOp",EDGE,"E6"),sQuery(id+"F0.wireOp",EDGE,"E7"),sQuery(id+"F0.wireOp",EDGE,"E8"),sQuery(id+"F0.wireOp",EDGE,"E9"),sQuery(id+"F0.wireOp",EDGE,"E10")])],"isStart":false});Q2=makeQuery(id+"F7.boolean.opBoolean","INTERSECT",EDGE,{"derivedFrom":[makeQuery(id+"F4.boolean.opBoolean","MERGE",FACE,{"derivedFrom":[subQ0,makeQuery(id+"F4.opPattern","COPY",FACE,{"derivedFrom":subQ0,"instanceName":"1"}),makeQuery(id+"F4.opPattern","COPY",FACE,{"derivedFrom":subQ0,"instanceName":"2"}),makeQuery(id+"F4.opPattern","COPY",FACE,{"derivedFrom":subQ0,"instanceName":"3"}),makeQuery(id+"F4.opPattern","COPY",FACE,{"derivedFrom":subQ0,"instanceName":"4"}),makeQuery(id+"F4.opPattern","COPY",FACE,{"derivedFrom":subQ0,"instanceName":"5"}),makeQuery(id+"F4.opPattern","COPY",FACE,{"derivedFrom":subQ0,"instanceName":"6"}),makeQuery(id+"F4.opPattern","COPY",FACE,{"derivedFrom":subQ0,"instanceName":"7"}),makeQuery(id+"F4.opPattern","COPY",FACE,{"derivedFrom":subQ0,"instanceName":"8"}),makeQuery(id+"F4.opPattern","COPY",FACE,{"derivedFrom":subQ0,"instanceName":"9"}),makeQuery(id+"F4.opPattern","COPY",FACE,{"derivedFrom":subQ0,"instanceName":"10"}),makeQuery(id+"F4.opPattern","COPY",FACE,{"derivedFrom":subQ0,"instanceName":"11"}),makeQuery(id+"F4.opPattern","COPY",FACE,{"derivedFrom":subQ0,"instanceName":"12"}),makeQuery(id+"F4.opPattern","COPY",FACE,{"derivedFrom":subQ0,"instanceName":"13"}),makeQuery(id+"F4.opPattern","COPY",FACE,{"derivedFrom":subQ0,"instanceName":"14"}),makeQuery(id+"F4.opPattern","COPY",FACE,{"derivedFrom":subQ0,"instanceName":"15"}),makeQuery(id+"F4.opPattern","COPY",FACE,{"derivedFrom":subQ0,"instanceName":"16"}),makeQuery(id+"F4.opPattern","COPY",FACE,{"derivedFrom":subQ0,"instanceName":"17"}),makeQuery(id+"F4.opPattern","COPY",FACE,{"derivedFrom":subQ0,"instanceName":"18"}),makeQuery(id+"F4.opPattern","COPY",FACE,{"derivedFrom":subQ0,"instanceName":"19"}),makeQuery(id+"F4.opPattern","COPY",FACE,{"derivedFrom":subQ0,"instanceName":"20"}),makeQuery(id+"F4.opPattern","COPY",FACE,{"derivedFrom":subQ0,"instanceName":"21"}),makeQuery(id+"F4.opPattern","COPY",FACE,{"derivedFrom":subQ0,"instanceName":"22"}),makeQuery(id+"F4.opPattern","COPY",FACE,{"derivedFrom":subQ0,"instanceName":"23"}),makeQuery(id+"F4.opPattern","COPY",FACE,{"derivedFrom":subQ0,"instanceName":"24"}),makeQuery(id+"F4.opPattern","COPY",FACE,{"derivedFrom":subQ0,"instanceName":"25"}),makeQuery(id+"F4.opPattern","COPY",FACE,{"derivedFrom":subQ0,"instanceName":"26"}),makeQuery(id+"F4.opPattern","COPY",FACE,{"derivedFrom":subQ0,"instanceName":"27"}),makeQuery(id+"F4.opPattern","COPY",FACE,{"derivedFrom":subQ0,"instanceName":"28"}),makeQuery(id+"F4.opPattern","COPY",FACE,{"derivedFrom":subQ0,"instanceName":"29"}),makeQuery(id+"F4.opPattern","COPY",FACE,{"derivedFrom":subQ0,"instanceName":"30"}),makeQuery(id+"F4.opPattern","COPY",FACE,{"derivedFrom":subQ0,"instanceName":"31"}),makeQuery(id+"F4.opPattern","COPY",FACE,{"derivedFrom":subQ0,"instanceName":"32"}),makeQuery(id+"F4.opPattern","COPY",FACE,{"derivedFrom":subQ0,"instanceName":"33"}),makeQuery(id+"F4.opPattern","COPY",FACE,{"derivedFrom":subQ0,"instanceName":"34"}),makeQuery(id+"F4.opPattern","COPY",FACE,{"derivedFrom":subQ0,"instanceName":"35"}),makeQuery(id+"F4.opPattern","COPY",FACE,{"derivedFrom":subQ0,"instanceName":"36"}),makeQuery(id+"F4.opPattern","COPY",FACE,{"derivedFrom":subQ0,"instanceName":"37"}),makeQuery(id+"F4.opPattern","COPY",FACE,{"derivedFrom":subQ0,"instanceName":"38"}),makeQuery(id+"F4.opPattern","COPY",FACE,{"derivedFrom":subQ0,"instanceName":"39"}),makeQuery(id+"F4.opPattern","COPY",FACE,{"derivedFrom":subQ0,"instanceName":"40"}),makeQuery(id+"F4.opPattern","COPY",FACE,{"derivedFrom":subQ0,"instanceName":"41"}),makeQuery(id+"F4.opPattern","COPY",FACE,{"derivedFrom":subQ0,"instanceName":"42"}),makeQuery(id+"F4.opPattern","COPY",FACE,{"derivedFrom":subQ0,"instanceName":"43"}),makeQuery(id+"F4.opPattern","COPY",FACE,{"derivedFrom":subQ0,"instanceName":"44"}),makeQuery(id+"F4.opPattern","COPY",FACE,{"derivedFrom":subQ0,"instanceName":"45"}),makeQuery(id+"F4.opPattern","COPY",FACE,{"derivedFrom":subQ0,"instanceName":"46"}),makeQuery(id+"F4.opPattern","COPY",FACE,{"derivedFrom":subQ0,"instanceName":"47"})]}),makeQuery(id+"F7.opExtrude","SWEPT_FACE",FACE,{"disambiguationData":[OSD([sQuery(id+"F0.wireOp",EDGE,"E15")])]})]});}
            var Q3;
            {var subQ0=makeQuery(id+"F1.opExtrude","CAP_FACE",FACE,{"disambiguationData":[OSD([sQuery(id+"F0.wireOp",EDGE,"E5"),sQuery(id+"F0.wireOp",EDGE,"E6"),sQuery(id+"F0.wireOp",EDGE,"E7"),sQuery(id+"F0.wireOp",EDGE,"E8"),sQuery(id+"F0.wireOp",EDGE,"E9"),sQuery(id+"F0.wireOp",EDGE,"E10")])],"isStart":false});Q3=makeQuery(id+"F7.boolean.opBoolean","INTERSECT",EDGE,{"derivedFrom":[makeQuery(id+"F4.boolean.opBoolean","MERGE",FACE,{"derivedFrom":[subQ0,makeQuery(id+"F4.opPattern","COPY",FACE,{"derivedFrom":subQ0,"instanceName":"1"}),makeQuery(id+"F4.opPattern","COPY",FACE,{"derivedFrom":subQ0,"instanceName":"2"}),makeQuery(id+"F4.opPattern","COPY",FACE,{"derivedFrom":subQ0,"instanceName":"3"}),makeQuery(id+"F4.opPattern","COPY",FACE,{"derivedFrom":subQ0,"instanceName":"4"}),makeQuery(id+"F4.opPattern","COPY",FACE,{"derivedFrom":subQ0,"instanceName":"5"}),makeQuery(id+"F4.opPattern","COPY",FACE,{"derivedFrom":subQ0,"instanceName":"6"}),makeQuery(id+"F4.opPattern","COPY",FACE,{"derivedFrom":subQ0,"instanceName":"7"}),makeQuery(id+"F4.opPattern","COPY",FACE,{"derivedFrom":subQ0,"instanceName":"8"}),makeQuery(id+"F4.opPattern","COPY",FACE,{"derivedFrom":subQ0,"instanceName":"9"}),makeQuery(id+"F4.opPattern","COPY",FACE,{"derivedFrom":subQ0,"instanceName":"10"}),makeQuery(id+"F4.opPattern","COPY",FACE,{"derivedFrom":subQ0,"instanceName":"11"}),makeQuery(id+"F4.opPattern","COPY",FACE,{"derivedFrom":subQ0,"instanceName":"12"}),makeQuery(id+"F4.opPattern","COPY",FACE,{"derivedFrom":subQ0,"instanceName":"13"}),makeQuery(id+"F4.opPattern","COPY",FACE,{"derivedFrom":subQ0,"instanceName":"14"}),makeQuery(id+"F4.opPattern","COPY",FACE,{"derivedFrom":subQ0,"instanceName":"15"}),makeQuery(id+"F4.opPattern","COPY",FACE,{"derivedFrom":subQ0,"instanceName":"16"}),makeQuery(id+"F4.opPattern","COPY",FACE,{"derivedFrom":subQ0,"instanceName":"17"}),makeQuery(id+"F4.opPattern","COPY",FACE,{"derivedFrom":subQ0,"instanceName":"18"}),makeQuery(id+"F4.opPattern","COPY",FACE,{"derivedFrom":subQ0,"instanceName":"19"}),makeQuery(id+"F4.opPattern","COPY",FACE,{"derivedFrom":subQ0,"instanceName":"20"}),makeQuery(id+"F4.opPattern","COPY",FACE,{"derivedFrom":subQ0,"instanceName":"21"}),makeQuery(id+"F4.opPattern","COPY",FACE,{"derivedFrom":subQ0,"instanceName":"22"}),makeQuery(id+"F4.opPattern","COPY",FACE,{"derivedFrom":subQ0,"instanceName":"23"}),makeQuery(id+"F4.opPattern","COPY",FACE,{"derivedFrom":subQ0,"instanceName":"24"}),makeQuery(id+"F4.opPattern","COPY",FACE,{"derivedFrom":subQ0,"instanceName":"25"}),makeQuery(id+"F4.opPattern","COPY",FACE,{"derivedFrom":subQ0,"instanceName":"26"}),makeQuery(id+"F4.opPattern","COPY",FACE,{"derivedFrom":subQ0,"instanceName":"27"}),makeQuery(id+"F4.opPattern","COPY",FACE,{"derivedFrom":subQ0,"instanceName":"28"}),makeQuery(id+"F4.opPattern","COPY",FACE,{"derivedFrom":subQ0,"instanceName":"29"}),makeQuery(id+"F4.opPattern","COPY",FACE,{"derivedFrom":subQ0,"instanceName":"30"}),makeQuery(id+"F4.opPattern","COPY",FACE,{"derivedFrom":subQ0,"instanceName":"31"}),makeQuery(id+"F4.opPattern","COPY",FACE,{"derivedFrom":subQ0,"instanceName":"32"}),makeQuery(id+"F4.opPattern","COPY",FACE,{"derivedFrom":subQ0,"instanceName":"33"}),makeQuery(id+"F4.opPattern","COPY",FACE,{"derivedFrom":subQ0,"instanceName":"34"}),makeQuery(id+"F4.opPattern","COPY",FACE,{"derivedFrom":subQ0,"instanceName":"35"}),makeQuery(id+"F4.opPattern","COPY",FACE,{"derivedFrom":subQ0,"instanceName":"36"}),makeQuery(id+"F4.opPattern","COPY",FACE,{"derivedFrom":subQ0,"instanceName":"37"}),makeQuery(id+"F4.opPattern","COPY",FACE,{"derivedFrom":subQ0,"instanceName":"38"}),makeQuery(id+"F4.opPattern","COPY",FACE,{"derivedFrom":subQ0,"instanceName":"39"}),makeQuery(id+"F4.opPattern","COPY",FACE,{"derivedFrom":subQ0,"instanceName":"40"}),makeQuery(id+"F4.opPattern","COPY",FACE,{"derivedFrom":subQ0,"instanceName":"41"}),makeQuery(id+"F4.opPattern","COPY",FACE,{"derivedFrom":subQ0,"instanceName":"42"}),makeQuery(id+"F4.opPattern","COPY",FACE,{"derivedFrom":subQ0,"instanceName":"43"}),makeQuery(id+"F4.opPattern","COPY",FACE,{"derivedFrom":subQ0,"instanceName":"44"}),makeQuery(id+"F4.opPattern","COPY",FACE,{"derivedFrom":subQ0,"instanceName":"45"}),makeQuery(id+"F4.opPattern","COPY",FACE,{"derivedFrom":subQ0,"instanceName":"46"}),makeQuery(id+"F4.opPattern","COPY",FACE,{"derivedFrom":subQ0,"instanceName":"47"})]}),makeQuery(id+"F7.opExtrude","SWEPT_FACE",FACE,{"disambiguationData":[OSD([sQuery(id+"F0.wireOp",EDGE,"E16")])]})]});}
            var Q4;
            Q4=makeQuery(id+"F11.boolean.opBoolean","COPY",EDGE,{"derivedFrom":makeQuery(id+"F11.opExtrude","CAP_EDGE",EDGE,{"disambiguationData":[OSD([sQuery(id+"F8.wireOp",EDGE,"E22")])],"isStart":true})});
            var Q5;
            {var subQ0=makeQuery(id+"F1.opExtrude","CAP_FACE",FACE,{"disambiguationData":[OSD([sQuery(id+"F0.wireOp",EDGE,"E5"),sQuery(id+"F0.wireOp",EDGE,"E6"),sQuery(id+"F0.wireOp",EDGE,"E7"),sQuery(id+"F0.wireOp",EDGE,"E8"),sQuery(id+"F0.wireOp",EDGE,"E9"),sQuery(id+"F0.wireOp",EDGE,"E10")])],"isStart":true});Q5=makeQuery(id+"F11.boolean.opBoolean","INTERSECT",EDGE,{"derivedFrom":[makeQuery(id+"F4.boolean.opBoolean","MERGE",FACE,{"derivedFrom":[subQ0,makeQuery(id+"F4.opPattern","COPY",FACE,{"derivedFrom":subQ0,"instanceName":"1"}),makeQuery(id+"F4.opPattern","COPY",FACE,{"derivedFrom":subQ0,"instanceName":"2"}),makeQuery(id+"F4.opPattern","COPY",FACE,{"derivedFrom":subQ0,"instanceName":"3"}),makeQuery(id+"F4.opPattern","COPY",FACE,{"derivedFrom":subQ0,"instanceName":"4"}),makeQuery(id+"F4.opPattern","COPY",FACE,{"derivedFrom":subQ0,"instanceName":"5"}),makeQuery(id+"F4.opPattern","COPY",FACE,{"derivedFrom":subQ0,"instanceName":"6"}),makeQuery(id+"F4.opPattern","COPY",FACE,{"derivedFrom":subQ0,"instanceName":"7"}),makeQuery(id+"F4.opPattern","COPY",FACE,{"derivedFrom":subQ0,"instanceName":"8"}),makeQuery(id+"F4.opPattern","COPY",FACE,{"derivedFrom":subQ0,"instanceName":"9"}),makeQuery(id+"F4.opPattern","COPY",FACE,{"derivedFrom":subQ0,"instanceName":"10"}),makeQuery(id+"F4.opPattern","COPY",FACE,{"derivedFrom":subQ0,"instanceName":"11"}),makeQuery(id+"F4.opPattern","COPY",FACE,{"derivedFrom":subQ0,"instanceName":"12"}),makeQuery(id+"F4.opPattern","COPY",FACE,{"derivedFrom":subQ0,"instanceName":"13"}),makeQuery(id+"F4.opPattern","COPY",FACE,{"derivedFrom":subQ0,"instanceName":"14"}),makeQuery(id+"F4.opPattern","COPY",FACE,{"derivedFrom":subQ0,"instanceName":"15"}),makeQuery(id+"F4.opPattern","COPY",FACE,{"derivedFrom":subQ0,"instanceName":"16"}),makeQuery(id+"F4.opPattern","COPY",FACE,{"derivedFrom":subQ0,"instanceName":"17"}),makeQuery(id+"F4.opPattern","COPY",FACE,{"derivedFrom":subQ0,"instanceName":"18"}),makeQuery(id+"F4.opPattern","COPY",FACE,{"derivedFrom":subQ0,"instanceName":"19"}),makeQuery(id+"F4.opPattern","COPY",FACE,{"derivedFrom":subQ0,"instanceName":"20"}),makeQuery(id+"F4.opPattern","COPY",FACE,{"derivedFrom":subQ0,"instanceName":"21"}),makeQuery(id+"F4.opPattern","COPY",FACE,{"derivedFrom":subQ0,"instanceName":"22"}),makeQuery(id+"F4.opPattern","COPY",FACE,{"derivedFrom":subQ0,"instanceName":"23"}),makeQuery(id+"F4.opPattern","COPY",FACE,{"derivedFrom":subQ0,"instanceName":"24"}),makeQuery(id+"F4.opPattern","COPY",FACE,{"derivedFrom":subQ0,"instanceName":"25"}),makeQuery(id+"F4.opPattern","COPY",FACE,{"derivedFrom":subQ0,"instanceName":"26"}),makeQuery(id+"F4.opPattern","COPY",FACE,{"derivedFrom":subQ0,"instanceName":"27"}),makeQuery(id+"F4.opPattern","COPY",FACE,{"derivedFrom":subQ0,"instanceName":"28"}),makeQuery(id+"F4.opPattern","COPY",FACE,{"derivedFrom":subQ0,"instanceName":"29"}),makeQuery(id+"F4.opPattern","COPY",FACE,{"derivedFrom":subQ0,"instanceName":"30"}),makeQuery(id+"F4.opPattern","COPY",FACE,{"derivedFrom":subQ0,"instanceName":"31"}),makeQuery(id+"F4.opPattern","COPY",FACE,{"derivedFrom":subQ0,"instanceName":"32"}),makeQuery(id+"F4.opPattern","COPY",FACE,{"derivedFrom":subQ0,"instanceName":"33"}),makeQuery(id+"F4.opPattern","COPY",FACE,{"derivedFrom":subQ0,"instanceName":"34"}),makeQuery(id+"F4.opPattern","COPY",FACE,{"derivedFrom":subQ0,"instanceName":"35"}),makeQuery(id+"F4.opPattern","COPY",FACE,{"derivedFrom":subQ0,"instanceName":"36"}),makeQuery(id+"F4.opPattern","COPY",FACE,{"derivedFrom":subQ0,"instanceName":"37"}),makeQuery(id+"F4.opPattern","COPY",FACE,{"derivedFrom":subQ0,"instanceName":"38"}),makeQuery(id+"F4.opPattern","COPY",FACE,{"derivedFrom":subQ0,"instanceName":"39"}),makeQuery(id+"F4.opPattern","COPY",FACE,{"derivedFrom":subQ0,"instanceName":"40"}),makeQuery(id+"F4.opPattern","COPY",FACE,{"derivedFrom":subQ0,"instanceName":"41"}),makeQuery(id+"F4.opPattern","COPY",FACE,{"derivedFrom":subQ0,"instanceName":"42"}),makeQuery(id+"F4.opPattern","COPY",FACE,{"derivedFrom":subQ0,"instanceName":"43"}),makeQuery(id+"F4.opPattern","COPY",FACE,{"derivedFrom":subQ0,"instanceName":"44"}),makeQuery(id+"F4.opPattern","COPY",FACE,{"derivedFrom":subQ0,"instanceName":"45"}),makeQuery(id+"F4.opPattern","COPY",FACE,{"derivedFrom":subQ0,"instanceName":"46"}),makeQuery(id+"F4.opPattern","COPY",FACE,{"derivedFrom":subQ0,"instanceName":"47"})]}),makeQuery(id+"F11.opExtrude","SWEPT_FACE",FACE,{"disambiguationData":[OSD([sQuery(id+"F8.wireOp",EDGE,"E22")])]})]});}
            var Q6;
            Q6=makeQuery(id+"F14.boolean.opBoolean","INTERSECT",EDGE,{"disambiguationData":[OD(1.0)],"derivedFrom":[makeQuery(id+"F6.opExtrude","SWEPT_FACE",FACE,{"disambiguationData":[OSD([sQuery(id+"F5.wireOp",EDGE,"E17")])]}),makeQuery(id+"F14.opExtrude","SWEPT_FACE",FACE,{"disambiguationData":[OSD([sQuery(id+"F13.wireOp",EDGE,"E26")])]})]});
            var Q7;
            Q7=makeQuery(id+"F14.boolean.opBoolean","INTERSECT",EDGE,{"disambiguationData":[OD(0.0)],"derivedFrom":[makeQuery(id+"F6.opExtrude","SWEPT_FACE",FACE,{"disambiguationData":[OSD([sQuery(id+"F5.wireOp",EDGE,"E17")])]}),makeQuery(id+"F14.opExtrude","SWEPT_FACE",FACE,{"disambiguationData":[OSD([sQuery(id+"F13.wireOp",EDGE,"E26")])]})]});
            var Q8;
            Q8=makeQuery(id+"F7.boolean.opBoolean","COPY",EDGE,{"derivedFrom":makeQuery(id+"F7.opExtrude","CAP_EDGE",EDGE,{"disambiguationData":[OSD([sQuery(id+"F0.wireOp",EDGE,"E15")])],"isStart":false})});
            var Q9;
            Q9=makeQuery(id+"F7.boolean.opBoolean","COPY",EDGE,{"derivedFrom":makeQuery(id+"F7.opExtrude","CAP_EDGE",EDGE,{"disambiguationData":[OSD([sQuery(id+"F0.wireOp",EDGE,"E16")])],"isStart":false})});
            var Q10;
            Q10=makeQuery(id+"F6.opExtrude","CAP_EDGE",EDGE,{"disambiguationData":[OSD([sQuery(id+"F5.wireOp",EDGE,"E17")])],"isStart":false});
            fillet(context, id + "F15", {"entities" : qUnion([Q0, Q1, Q2, Q3, Q4, Q5, Q6, Q7, Q8, Q9, Q10]), "radius" : 0.5 * mm, "tangentPropagation" : true, "allowEdgeOverflow" : false});
        }
    });
